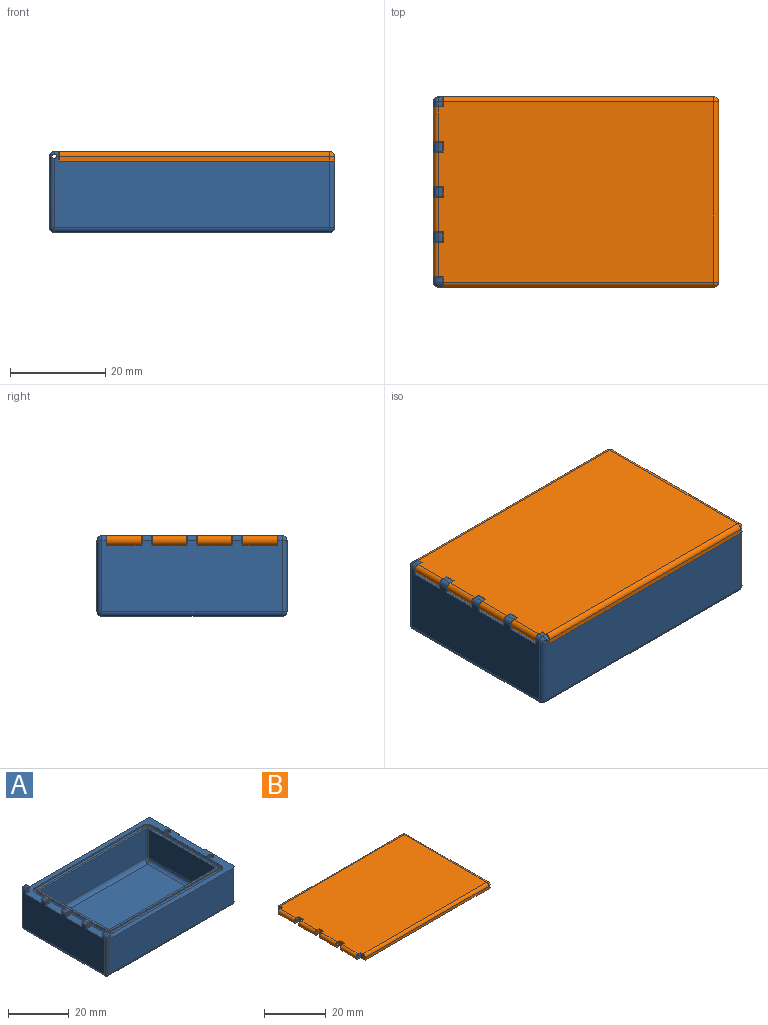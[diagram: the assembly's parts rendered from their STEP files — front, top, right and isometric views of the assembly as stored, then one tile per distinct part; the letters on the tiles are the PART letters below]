
ASSEMBLY  parts=2 mates=1
PART A: 99 faces, bbox 60x40x17 mm
  f0: plane 60.01x40.01mm, normal (0,0,1), area 382.4mm2, adj f1,f12,f15,f18,f21,f24,f27,f30
  f1: plane 38x14mm, normal (1,0,0), area 503.7mm2, adj f0,f63,f65,f66,f88
  f2: plane 51.5x33.5mm, normal (0,0,1), area 125.3mm2, adj f3,f4,f5,f6,f8,f10,f13,f16
  f3: plane 30.5x11.5mm, normal (1,0,0), area 350.7mm2, adj f2,f84,f87,f96
  f4: plane 48.5x11.5mm, normal (0,1,0), area 557.8mm2, adj f2,f84,f85,f97
  f5: plane 30.5x11.5mm, normal (-1,0,0), area 350.7mm2, adj f2,f85,f86,f93
  f6: plane 48.5x11.5mm, normal (0,-1,0), area 557.8mm2, adj f2,f86,f87,f92
  f7: plane 47x29mm, normal (0,0,1), area 1363mm2, adj f92,f93,f96,f97
  f8: cylinder r=0.75mm len=0.75mm, axis (0,0,1), area 0.6mm2, adj f2,f9,f10,f28
  f9: torus R=1.5mm, axis (0,0,1), area 5.6mm2, adj f8,f11,f29,f31
  f10: plane 50x0.5mm, normal (0,-1,0), area 25mm2, adj f2,f8,f11,f13
  f11: cylinder r=0.75mm len=50mm, axis (1,0,0), area 117.8mm2, adj f9,f10,f12,f14
  f12: plane 50x0.5mm, normal (0,1,0), area 25mm2, adj f0,f11,f15,f31
  f13: cylinder r=0.75mm len=0.75mm, axis (0,0,1), area 0.6mm2, adj f2,f10,f14,f16
  f14: torus R=1.5mm, axis (0,0,1), area 5.6mm2, adj f11,f13,f15,f17
  f15: cylinder r=2.25mm len=2.25mm, axis (0,0,1), area 1.8mm2, adj f0,f12,f14,f18
  f16: plane 32x0.5mm, normal (-1,0,0), area 16mm2, adj f2,f13,f17,f19
  f17: cylinder r=0.75mm len=32mm, axis (0,-1,0), area 75.4mm2, adj f14,f16,f18,f20
  f18: plane 32x0.5mm, normal (1,0,0), area 16mm2, adj f0,f15,f17,f21
  f19: cylinder r=0.75mm len=0.75mm, axis (0,0,1), area 0.6mm2, adj f2,f16,f20,f22
  f20: torus R=1.5mm, axis (0,0,1), area 5.6mm2, adj f17,f19,f21,f23
  f21: cylinder r=2.25mm len=2.25mm, axis (0,0,1), area 1.8mm2, adj f0,f18,f20,f24
  f22: plane 50x0.5mm, normal (0,1,0), area 25mm2, adj f2,f19,f23,f25
  f23: cylinder r=0.75mm len=50mm, axis (-1,0,0), area 117.8mm2, adj f20,f22,f24,f26
  f24: plane 50x0.5mm, normal (0,-1,0), area 25mm2, adj f0,f21,f23,f27
  f25: cylinder r=0.75mm len=0.75mm, axis (0,0,1), area 0.6mm2, adj f2,f22,f26,f28
  f26: torus R=1.5mm, axis (0,0,1), area 5.6mm2, adj f23,f25,f27,f29
  f27: cylinder r=2.25mm len=2.25mm, axis (0,0,1), area 1.8mm2, adj f0,f24,f26,f30
  f28: plane 32x0.5mm, normal (1,0,0), area 16mm2, adj f2,f8,f25,f29
  f29: cylinder r=0.75mm len=32mm, axis (0,1,0), area 75.4mm2, adj f9,f26,f28,f30
  f30: plane 32x0.5mm, normal (-1,0,0), area 16mm2, adj f0,f27,f29,f31
  f31: cylinder r=2.25mm len=2.25mm, axis (0,0,1), area 1.8mm2, adj f0,f9,f12,f30
  f32: plane 58x38mm, normal (0,0,-1), area 2204mm2, adj f66,f67,f71,f72
  f33: plane 58x15mm, normal (0,1,0), area 812.8mm2, adj f0,f41,f62,f63,f67,f68,f78
  f34: plane 58x15mm, normal (0,-1,0), area 812.8mm2, adj f0,f56,f58,f65,f71,f74,f77
  f35: plane 38x15mm, normal (-1,0,0), area 540mm2, adj f0,f40,f43,f44,f47,f48,f51,f52
  f36: cylinder r=1mm len=2mm, axis (0,0,1), area 6.3mm2, adj f0,f37
  f37: plane 2x2mm, normal (0,0,1), area 3.1mm2, adj f36
  f38: cylinder r=1mm len=2mm, axis (0,0,1), area 6.3mm2, adj f0,f39
  f39: plane 2x2mm, normal (0,0,1), area 3.1mm2, adj f38
  f40: plane 2x2mm, normal (0,-1,0), area 3mm2, adj f0,f35,f41,f42,f62,f79
  f41: plane 2x2mm, normal (1,0,0), area 3.8mm2, adj f0,f33,f40,f42,f78
  f42: plane 1x1mm, normal (0,0,1), area 1mm2, adj f40,f41,f78,f79
  f43: plane 2x2mm, normal (0,1,0), area 3mm2, adj f0,f35,f45,f46,f61,f83
  f44: plane 2x2mm, normal (0,-1,0), area 3mm2, adj f0,f35,f45,f46,f61,f83
  f45: plane 2x2mm, normal (1,0,0), area 4mm2, adj f0,f43,f44,f46
  f46: plane 2x1mm, normal (0,0,1), area 2mm2, adj f43,f44,f45,f83
  f47: plane 2x2mm, normal (0,1,0), area 3mm2, adj f0,f35,f49,f50,f60,f82
  f48: plane 2x2mm, normal (0,-1,0), area 3mm2, adj f0,f35,f49,f50,f60,f82
  f49: plane 2x2mm, normal (1,0,0), area 4mm2, adj f0,f47,f48,f50
  f50: plane 2x1mm, normal (0,0,1), area 2mm2, adj f47,f48,f49,f82
  f51: plane 2x2mm, normal (0,1,0), area 3mm2, adj f0,f35,f53,f54,f59,f81
  f52: plane 2x2mm, normal (0,-1,0), area 3mm2, adj f0,f35,f53,f54,f59,f81
  f53: plane 2x2mm, normal (1,0,0), area 4mm2, adj f0,f51,f52,f54
  f54: plane 2x1mm, normal (0,0,1), area 2mm2, adj f51,f52,f53,f81
  f55: plane 2x2mm, normal (0,1,0), area 3mm2, adj f0,f35,f56,f57,f58,f75
  f56: plane 2x2mm, normal (1,0,0), area 3.8mm2, adj f0,f34,f55,f57,f77
  f57: plane 1x1mm, normal (0,0,1), area 1mm2, adj f55,f56,f75,f77
  f58: cylinder r=0.5mm len=2mm, axis (0,-1,0), area 6.1mm2, adj f34,f55,f74,f76,f77
  f59: cylinder r=0.5mm len=2mm, axis (0,-1,0), area 6.3mm2, adj f51,f52
  f60: cylinder r=0.5mm len=2mm, axis (0,-1,0), area 6.3mm2, adj f47,f48
  f61: cylinder r=0.5mm len=2mm, axis (0,-1,0), area 6.3mm2, adj f43,f44
  f62: cylinder r=0.5mm len=2mm, axis (0,-1,0), area 6.1mm2, adj f33,f40,f68,f78,f80
  f63: cylinder r=1mm len=14mm, axis (0,0,1), area 22mm2, adj f0,f1,f33,f64
  f64: sphere r=1mm, area 1.6mm2, adj f63,f66,f67
  f65: cylinder r=1mm len=14mm, axis (0,0,-1), area 22mm2, adj f0,f1,f34,f69
  f66: cylinder r=1mm len=38mm, axis (0,1,0), area 59.7mm2, adj f1,f32,f64,f69
  f67: cylinder r=1mm len=58mm, axis (-1,0,0), area 91.1mm2, adj f32,f33,f64,f70
  f68: cylinder r=1mm len=15mm, axis (0,0,-1), area 23.4mm2, adj f33,f35,f62,f70,f80
  f69: sphere r=1mm, area 1.6mm2, adj f65,f66,f71
  f70: sphere r=1mm, area 1.6mm2, adj f67,f68,f72
  f71: cylinder r=1mm len=58mm, axis (1,0,0), area 91.1mm2, adj f32,f34,f69,f73
  f72: cylinder r=1mm len=38mm, axis (0,-1,0), area 59.7mm2, adj f32,f35,f70,f73
  f73: sphere r=1mm, area 1.6mm2, adj f71,f72,f74
  f74: cylinder r=1mm len=15mm, axis (0,0,1), area 23.4mm2, adj f34,f35,f58,f73,f76
  f75: cylinder r=1mm len=1mm, axis (0,1,0), area 1.6mm2, adj f35,f55,f57,f76
  f76: sphere r=1mm, area 1.4mm2, adj f58,f74,f75,f77
  f77: cylinder r=1mm len=1mm, axis (-1,0,0), area 1.4mm2, adj f34,f56,f57,f58,f76
  f78: cylinder r=1mm len=1mm, axis (1,0,0), area 1.4mm2, adj f33,f41,f42,f62,f80
  f79: cylinder r=1mm len=1mm, axis (0,1,0), area 1.6mm2, adj f35,f40,f42,f80
  f80: sphere r=1mm, area 1.4mm2, adj f62,f68,f78,f79
  f81: cylinder r=1mm len=2mm, axis (0,1,0), area 3.1mm2, adj f35,f51,f52,f54
  f82: cylinder r=1mm len=2mm, axis (0,1,0), area 3.1mm2, adj f35,f47,f48,f50
  f83: cylinder r=1mm len=2mm, axis (0,1,0), area 3.1mm2, adj f35,f43,f44,f46
  f84: cylinder r=0.75mm len=11.5mm, axis (0,0,1), area 13.5mm2, adj f2,f3,f4,f98
  f85: cylinder r=0.75mm len=11.5mm, axis (0,0,-1), area 13.5mm2, adj f2,f4,f5,f95
  f86: cylinder r=0.75mm len=11.5mm, axis (0,0,1), area 13.5mm2, adj f2,f5,f6,f91
  f87: cylinder r=0.75mm len=11.5mm, axis (0,0,-1), area 13.5mm2, adj f2,f3,f6,f94
  f88: extruded ~12x3mm, area 3.6mm2, adj f0,f1,f90
  f89: plane 11.5x2.75mm, normal (1,0,0), area 24.7mm2, adj f0,f90
  f90: bspline ~12x3.16mm, area 5.6mm2, adj f0,f88,f89
  f91: bspline ~1.79x1.5mm, area 1.9mm2, adj f86,f92,f93
  f92: cylinder r=1.5mm len=48.5mm, axis (-1,0,0), area 113mm2, adj f6,f7,f91,f94
  f93: cylinder r=1.5mm len=30.5mm, axis (0,1,0), area 70.6mm2, adj f5,f7,f91,f95
  f94: bspline ~1.79x1.5mm, area 1.9mm2, adj f87,f92,f96
  f95: bspline ~1.79x1.5mm, area 1.9mm2, adj f85,f93,f97
  f96: cylinder r=1.5mm len=30.5mm, axis (0,-1,0), area 70.6mm2, adj f3,f7,f94,f98
  f97: cylinder r=1.5mm len=48.5mm, axis (1,0,0), area 113mm2, adj f4,f7,f95,f98
  f98: bspline ~1.79x1.5mm, area 1.9mm2, adj f84,f96,f97
PART B: 46 faces, bbox 60x40x4 mm
  f0: plane 56.9x1mm, normal (0,-1,0), area 56.9mm2, adj f3,f18,f38,f41
  f1: plane 56.9x1mm, normal (0,1,0), area 56.9mm2, adj f3,f21,f35,f36
  f2: plane 58x38mm, normal (0,0,1), area 2194.3mm2, adj f14,f15,f16,f18,f19,f20,f21,f22
  f3: plane 59x40mm, normal (0,0,-1), area 903.3mm2, adj f0,f1,f4,f5,f6,f7,f8,f10
  f4: plane 38x1mm, normal (1,0,0), area 38mm2, adj f3,f36,f39,f41
  f5: plane 27x2mm, normal (-1,0,0), area 54mm2, adj f3,f9,f10,f13
  f6: plane 45x2mm, normal (0,-1,0), area 90mm2, adj f3,f9,f10,f11
  f7: plane 27x2mm, normal (1,0,0), area 54mm2, adj f3,f9,f11,f12
  f8: plane 45x2mm, normal (0,1,0), area 90mm2, adj f3,f9,f12,f13
  f9: plane 48x30mm, normal (0,0,-1), area 1438.1mm2, adj f5,f6,f7,f8,f10,f11,f12,f13
  f10: cylinder r=1.5mm len=2mm, axis (0,0,1), area 4.7mm2, adj f3,f5,f6,f9
  f11: cylinder r=1.5mm len=2mm, axis (0,0,-1), area 4.7mm2, adj f3,f6,f7,f9
  f12: cylinder r=1.5mm len=2mm, axis (0,0,1), area 4.7mm2, adj f3,f7,f8,f9
  f13: cylinder r=1.5mm len=2mm, axis (0,0,-1), area 4.7mm2, adj f3,f5,f8,f9
  f14: plane 2.1x2mm, normal (0,-1,0), area 3mm2, adj f2,f3,f16,f17,f31
  f15: plane 2.1x2mm, normal (0,1,0), area 3mm2, adj f2,f3,f16,f29,f32
  f16: plane 2.2x2mm, normal (-1,0,0), area 4.4mm2, adj f2,f3,f14,f15
  f17: cylinder r=0.5mm len=7.3mm, axis (0,-1,0), area 22.9mm2, adj f14,f20
  f18: plane 2.1x2mm, normal (-1,0,0), area 4mm2, adj f0,f2,f3,f19,f38
  f19: plane 2.1x2mm, normal (0,-1,0), area 3mm2, adj f2,f3,f18,f30,f34
  f20: plane 2.1x2mm, normal (0,1,0), area 3mm2, adj f2,f3,f17,f21,f31
  f21: plane 2.1x2mm, normal (-1,0,0), area 4mm2, adj f1,f2,f3,f20,f35
  f22: plane 2.1x2mm, normal (0,-1,0), area 3mm2, adj f2,f3,f24,f25,f33
  f23: plane 2.1x2mm, normal (0,1,0), area 3mm2, adj f2,f3,f24,f30,f34
  f24: plane 2.2x2mm, normal (-1,0,0), area 4.4mm2, adj f2,f3,f22,f23
  f25: cylinder r=0.5mm len=7.3mm, axis (0,-1,0), area 22.9mm2, adj f22,f27
  f26: plane 2.1x2mm, normal (0,-1,0), area 3mm2, adj f2,f3,f28,f29,f32
  f27: plane 2.1x2mm, normal (0,1,0), area 3mm2, adj f2,f3,f25,f28,f33
  f28: plane 2.2x2mm, normal (-1,0,0), area 4.4mm2, adj f2,f3,f26,f27
  f29: cylinder r=0.5mm len=7.3mm, axis (0,-1,0), area 22.9mm2, adj f15,f26
  f30: cylinder r=0.5mm len=7.3mm, axis (0,-1,0), area 22.9mm2, adj f19,f23
  f31: cylinder r=1mm len=7.3mm, axis (0,1,0), area 22.9mm2, adj f2,f3,f14,f20
  f32: cylinder r=1mm len=7.3mm, axis (0,1,0), area 22.9mm2, adj f2,f3,f15,f26
  f33: cylinder r=1mm len=7.3mm, axis (0,1,0), area 22.9mm2, adj f2,f3,f22,f27
  f34: cylinder r=1mm len=7.3mm, axis (0,1,0), area 22.9mm2, adj f2,f3,f19,f23
  f35: cylinder r=1mm len=56.9mm, axis (1,0,0), area 89.4mm2, adj f1,f2,f21,f37
  f36: cylinder r=1mm len=1mm, axis (0,0,1), area 1.6mm2, adj f1,f3,f4,f37
  f37: sphere r=1mm, area 1.6mm2, adj f35,f36,f39
  f38: cylinder r=1mm len=56.9mm, axis (-1,0,0), area 89.4mm2, adj f0,f2,f18,f40
  f39: cylinder r=1mm len=38mm, axis (0,-1,0), area 59.7mm2, adj f2,f4,f37,f40
  f40: sphere r=1mm, area 1.6mm2, adj f38,f39,f41
  f41: cylinder r=1mm len=1mm, axis (0,0,-1), area 1.6mm2, adj f0,f3,f4,f40
  f42: cylinder r=1mm len=2mm, axis (0,0,-1), area 7.9mm2, adj f3,f43
  f43: plane 2x2mm, normal (0,0,-1), area 3.1mm2, adj f42
  f44: cylinder r=1mm len=2mm, axis (0,0,-1), area 7.9mm2, adj f3,f45
  f45: plane 2x2mm, normal (0,0,-1), area 3.1mm2, adj f44
PLACE A t=(-0.09,0.08,0.09)mm fixed
PLACE B rot(axis=(0,1,0),0deg) t=(-0.09,0.08,13.09)mm
MATE revolute B.f17 <-> A.f58  axis (0,-1,0) through (0.91,2.18,16.09)mm
